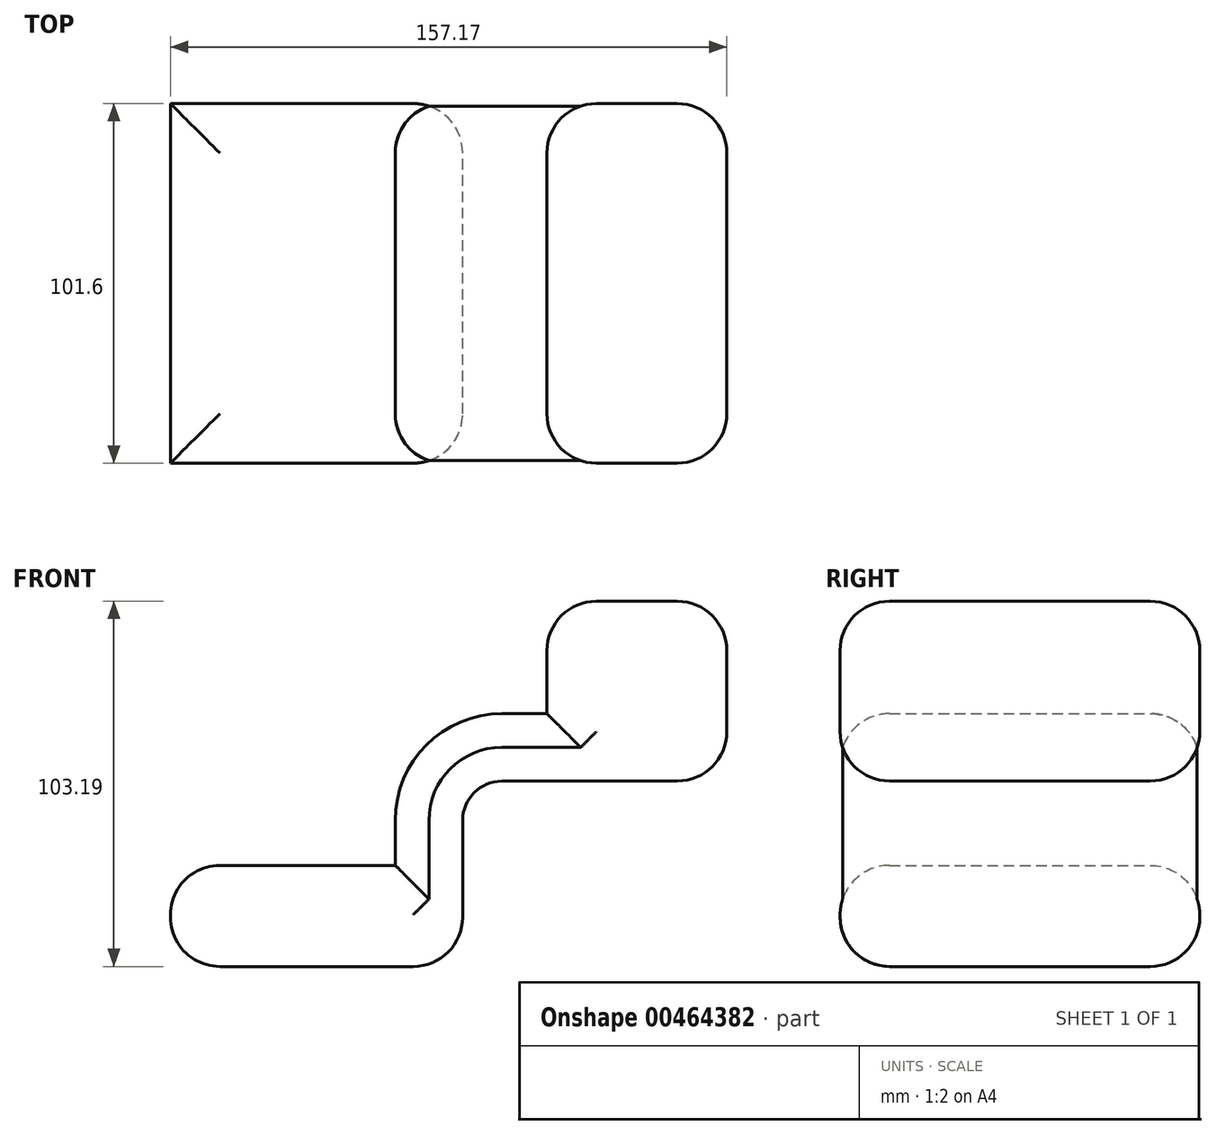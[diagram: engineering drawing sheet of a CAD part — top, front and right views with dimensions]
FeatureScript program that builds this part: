
annotation { "Feature Type Name" : "Feature", "Feature Type Description" : "" }
export const myFeature = defineFeature(function(context is Context, id is Id, definition is map)
    precondition{}
    {
        {
            var Q0;
            Q0=qCreatedBy(makeId("Front.planeOp"),FACE);
            var sketch = newSketch(context, id + "F0", { "sketchPlane" : qUnion([Q0])});
            skLineSegment(sketch, "E0.bottom", {"start": v(41.28, -14.29) * mm, "end": v(-41.28, -14.29) * mm});
            skLineSegment(sketch, "E0.top", {"start": v(22.23, 14.29) * mm, "end": v(-41.28, 14.29) * mm});
            skLineSegment(sketch, "E0.left", {"start": v(41.28, -14.29) * mm, "end": v(41.28, 14.29) * mm});
            skLineSegment(sketch, "E0.right", {"start": v(-41.28, -14.29) * mm, "end": v(-41.28, 14.29) * mm});
            skPoint(sketch, "E0.middle", {"position": v(0, 0) * mm});
            skLineSegment(sketch, "E1.bottom", {"start": v(115.89, 38.1) * mm, "end": v(65.09, 38.1) * mm});
            skLineSegment(sketch, "E1.top", {"start": v(115.89, 88.9) * mm, "end": v(65.09, 88.9) * mm});
            skLineSegment(sketch, "E1.left", {"start": v(115.89, 38.1) * mm, "end": v(115.89, 88.9) * mm});
            skLineSegment(sketch, "E1.right", {"start": v(65.09, 57.15) * mm, "end": v(65.09, 88.9) * mm});
            skPoint(sketch, "E1.middle", {"position": v(90.49, 63.5) * mm});
            skLineSegment(sketch, "E2", {"start": v(41.28, 14.29) * mm, "end": v(41.28, 26.99) * mm});
            skLineSegment(sketch, "E3", {"start": v(65.09, 38.1) * mm, "end": v(52.39, 38.1) * mm});
            skArc(sketch, "E4", {"start": v(41.28, 26.99) * mm, "mid": v(44.53, 34.85) * mm, "end": v(52.39, 38.1) * mm});
            skLineSegment(sketch, "E5.0", {"start": v(65.09, 57.15) * mm, "end": v(52.39, 57.15) * mm});
            skArc(sketch, "E5.1", {"start": v(22.23, 26.99) * mm, "mid": v(31.06, 48.32) * mm, "end": v(52.39, 57.15) * mm});
            skLineSegment(sketch, "E5.2", {"start": v(22.23, 14.29) * mm, "end": v(22.23, 26.99) * mm});
            skSolve(sketch);
        }
        {
            var Q0;
            Q0=makeQuery(id+"F0.imprint","IMPRINT",FACE,{"disambiguationData":[TD([[makeQuery(id+"F0.imprint","IMPRINT",EDGE,{"derivedFrom":sQuery(id+"F0.wireOp",EDGE,"E0.bottom")}),-1.0]])]});
            extrude(context, id + "F1", {"entities" : qUnion([Q0]), "depth" : 101.6 * mm});
        }
        {
            var Q0;
            Q0=makeQuery(id+"F1.opExtrude","CAP_EDGE",EDGE,{"disambiguationData":[OSD([sQuery(id+"F0.wireOp",EDGE,"E1.top")])],"isStart":false});
            var Q1;
            Q1=makeQuery(id+"F1.opExtrude","CAP_EDGE",EDGE,{"disambiguationData":[OSD([sQuery(id+"F0.wireOp",EDGE,"E1.right")])],"isStart":false});
            var Q2;
            Q2=makeQuery(id+"F1.opExtrude","SWEPT_EDGE",EDGE,{"disambiguationData":[OSD([sQuery(id+"F0.wireOp",EDGE,"E1.top"),sQuery(id+"F0.wireOp",EDGE,"E1.left")])]});
            var Q3;
            Q3=makeQuery(id+"F1.opExtrude","CAP_EDGE",EDGE,{"disambiguationData":[OSD([sQuery(id+"F0.wireOp",EDGE,"E1.top")])],"isStart":true});
            var Q4;
            Q4=makeQuery(id+"F1.opExtrude","CAP_EDGE",EDGE,{"disambiguationData":[OSD([sQuery(id+"F0.wireOp",EDGE,"E1.right")])],"isStart":true});
            var Q5;
            Q5=makeQuery(id+"F1.opExtrude","SWEPT_EDGE",EDGE,{"disambiguationData":[OSD([sQuery(id+"F0.wireOp",EDGE,"E1.top"),sQuery(id+"F0.wireOp",EDGE,"E1.right")])]});
            var Q6;
            Q6=makeQuery(id+"F1.opExtrude","CAP_EDGE",EDGE,{"disambiguationData":[OSD([sQuery(id+"F0.wireOp",EDGE,"E1.left")])],"isStart":false});
            var Q7;
            Q7=makeQuery(id+"F1.opExtrude","CAP_EDGE",EDGE,{"disambiguationData":[OSD([sQuery(id+"F0.wireOp",EDGE,"E1.left")])],"isStart":true});
            var Q8;
            Q8=makeQuery(id+"F1.opExtrude","SWEPT_EDGE",EDGE,{"disambiguationData":[OSD([sQuery(id+"F0.wireOp",EDGE,"E1.bottom"),sQuery(id+"F0.wireOp",EDGE,"E1.left")])]});
            var Q9;
            Q9=makeQuery(id+"F1.opExtrude","CAP_EDGE",EDGE,{"disambiguationData":[OSD([sQuery(id+"F0.wireOp",EDGE,"E1.bottom"),sQuery(id+"F0.wireOp",EDGE,"E3")])],"isStart":false});
            var Q10;
            Q10=makeQuery(id+"F1.opExtrude","CAP_EDGE",EDGE,{"disambiguationData":[OSD([sQuery(id+"F0.wireOp",EDGE,"E1.bottom"),sQuery(id+"F0.wireOp",EDGE,"E3")])],"isStart":true});
            var Q11;
            Q11=makeQuery(id+"F1.opExtrude","SWEPT_EDGE",EDGE,{"disambiguationData":[OSD([sQuery(id+"F0.wireOp",EDGE,"E0.bottom"),sQuery(id+"F0.wireOp",EDGE,"E0.left")])]});
            var Q12;
            Q12=makeQuery(id+"F1.opExtrude","CAP_EDGE",EDGE,{"disambiguationData":[OSD([sQuery(id+"F0.wireOp",EDGE,"E5.2")])],"isStart":false});
            var Q13;
            Q13=makeQuery(id+"F1.opExtrude","CAP_EDGE",EDGE,{"disambiguationData":[OSD([sQuery(id+"F0.wireOp",EDGE,"E0.top")])],"isStart":false});
            var Q14;
            Q14=makeQuery(id+"F1.opExtrude","SWEPT_EDGE",EDGE,{"disambiguationData":[OSD([sQuery(id+"F0.wireOp",EDGE,"E0.top"),sQuery(id+"F0.wireOp",EDGE,"E0.right")])]});
            var Q15;
            Q15=makeQuery(id+"F1.opExtrude","CAP_EDGE",EDGE,{"disambiguationData":[OSD([sQuery(id+"F0.wireOp",EDGE,"E0.top")])],"isStart":true});
            var Q16;
            Q16=makeQuery(id+"F1.opExtrude","CAP_EDGE",EDGE,{"disambiguationData":[OSD([sQuery(id+"F0.wireOp",EDGE,"E5.2")])],"isStart":true});
            var Q17;
            Q17=makeQuery(id+"F1.opExtrude","CAP_EDGE",EDGE,{"disambiguationData":[OSD([sQuery(id+"F0.wireOp",EDGE,"E0.bottom")])],"isStart":true});
            var Q18;
            Q18=makeQuery(id+"F1.opExtrude","SWEPT_EDGE",EDGE,{"disambiguationData":[OSD([sQuery(id+"F0.wireOp",EDGE,"E0.bottom"),sQuery(id+"F0.wireOp",EDGE,"E0.right")])]});
            var Q19;
            Q19=makeQuery(id+"F1.opExtrude","CAP_EDGE",EDGE,{"disambiguationData":[OSD([sQuery(id+"F0.wireOp",EDGE,"E0.bottom")])],"isStart":false});
            fillet(context, id + "F2", {"entities" : qUnion([Q0, Q1, Q2, Q3, Q4, Q5, Q6, Q7, Q8, Q9, Q10, Q11, Q12, Q13, Q14, Q15, Q16, Q17, Q18, Q19]), "radius" : 13.97 * mm, "tangentPropagation" : true, "allowEdgeOverflow" : false});
        }
    });
